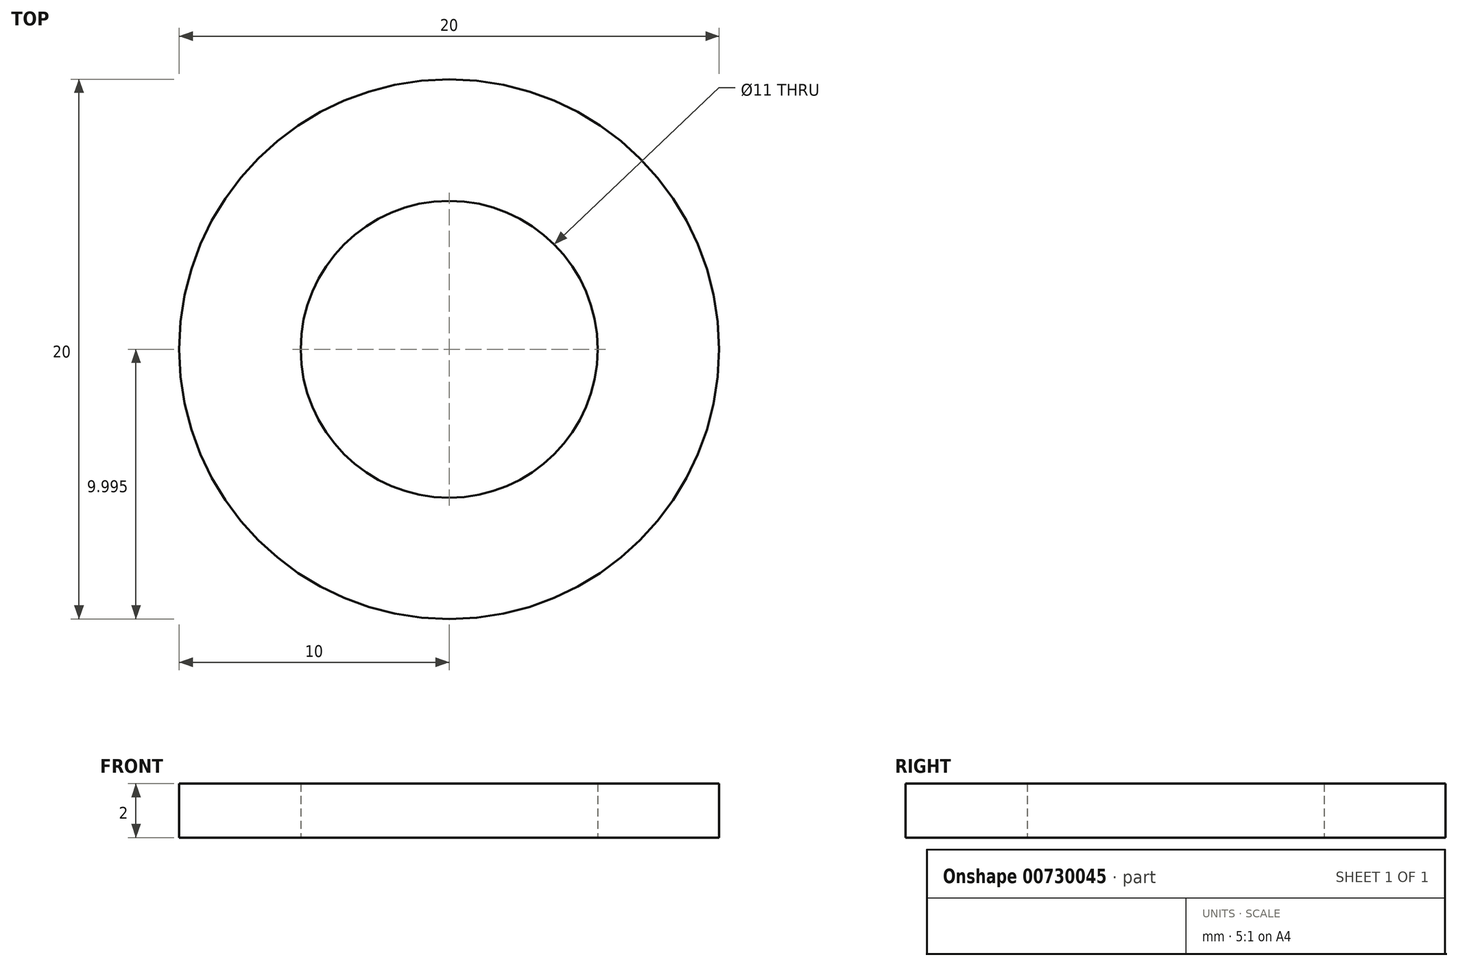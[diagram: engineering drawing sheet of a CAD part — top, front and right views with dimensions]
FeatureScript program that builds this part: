
annotation { "Feature Type Name" : "Feature", "Feature Type Description" : "" }
export const myFeature = defineFeature(function(context is Context, id is Id, definition is map)
    precondition{}
    {
        {
            var Q0;
            Q0=qCreatedBy(makeId("Top.planeOp"),FACE);
            var sketch = newSketch(context, id + "F0", { "sketchPlane" : qUnion([Q0])});
            skCircle(sketch, "E0", {"center": v(0, 13.6) * mm, "radius": 10 * mm});
            skCircle(sketch, "E1", {"center": v(0, 13.6) * mm, "radius": 5.5 * mm});
            skSolve(sketch);
        }
        {
            var Q0;
            Q0=makeQuery(id+"F0.imprint","IMPRINT",FACE,{"disambiguationData":[TD([[makeQuery(id+"F0.imprint","IMPRINT",EDGE,{"derivedFrom":sQuery(id+"F0.wireOp",EDGE,"E0")}),1.0]])]});
            extrude(context, id + "F1", {"entities" : qUnion([Q0]), "depth" : 2 * mm, "offsetDistance" : 25 * mm});
        }
    });
